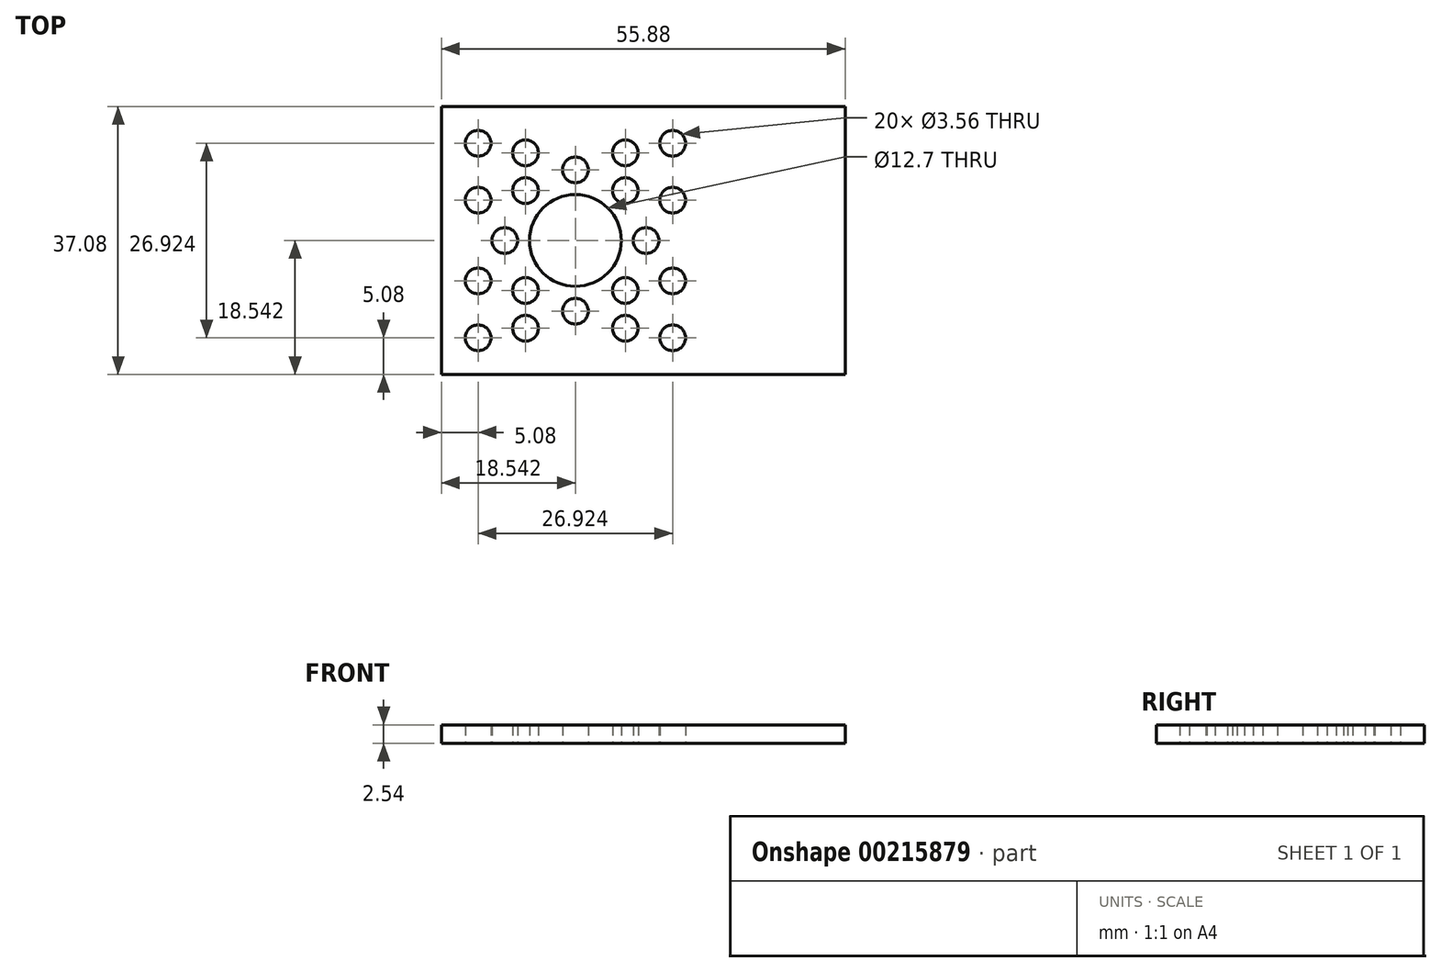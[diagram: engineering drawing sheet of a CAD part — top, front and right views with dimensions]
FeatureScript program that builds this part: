
annotation { "Feature Type Name" : "Feature", "Feature Type Description" : "" }
export const myFeature = defineFeature(function(context is Context, id is Id, definition is map)
    precondition{}
    {
        {
            var Q0;
            Q0=qCreatedBy(makeId("Top.planeOp"),FACE);
            var sketch = newSketch(context, id + "F0", { "sketchPlane" : qUnion([Q0])});
            skLineSegment(sketch, "E0.bottom", {"start": v(0, 0) * mm, "end": v(55.88, 0) * mm});
            skLineSegment(sketch, "E0.top", {"start": v(0, 37.08) * mm, "end": v(55.88, 37.08) * mm});
            skLineSegment(sketch, "E0.left", {"start": v(0, 0) * mm, "end": v(0, 37.08) * mm});
            skLineSegment(sketch, "E0.right", {"start": v(55.88, 0) * mm, "end": v(55.88, 37.08) * mm});
            skCircle(sketch, "E1", {"center": v(18.54, 18.54) * mm, "radius": 6.35 * mm});
            skCircle(sketch, "E2", {"center": v(18.54, 28.32) * mm, "radius": 1.78 * mm});
            skCircle(sketch, "E3", {"center": v(25.45, 30.68) * mm, "radius": 1.78 * mm});
            skCircle(sketch, "E4", {"center": v(25.45, 25.45) * mm, "radius": 1.78 * mm});
            skCircle(sketch, "E5", {"center": v(32, 32) * mm, "radius": 1.78 * mm});
            skCircle(sketch, "E6", {"center": v(32, 24.13) * mm, "radius": 1.78 * mm});
            skLineSegment(sketch, "E7", {"start": v(18.54, 18.54) * mm, "end": v(37.6, 18.54) * mm, "construction": true});
            skLineSegment(sketch, "E8", {"start": v(18.54, 18.54) * mm, "end": v(18.54, 10.07) * mm, "construction": true});
            skCircle(sketch, "E9.MirrorC", {"center": v(11.63, 30.68) * mm, "radius": 1.78 * mm});
            skCircle(sketch, "E10.MirrorC", {"center": v(5.08, 32) * mm, "radius": 1.78 * mm});
            skCircle(sketch, "E11.MirrorC", {"center": v(8.76, 18.54) * mm, "radius": 1.78 * mm});
            skCircle(sketch, "E12.MirrorC", {"center": v(11.63, 25.45) * mm, "radius": 1.78 * mm});
            skCircle(sketch, "E13.MirrorC", {"center": v(5.08, 24.13) * mm, "radius": 1.78 * mm});
            skCircle(sketch, "E14.MirrorC", {"center": v(5.08, 5.08) * mm, "radius": 1.78 * mm});
            skCircle(sketch, "E15.MirrorC", {"center": v(18.54, 8.76) * mm, "radius": 1.78 * mm});
            skCircle(sketch, "E16.MirrorC", {"center": v(11.63, 11.63) * mm, "radius": 1.78 * mm});
            skCircle(sketch, "E17.MirrorC", {"center": v(25.45, 6.4) * mm, "radius": 1.78 * mm});
            skCircle(sketch, "E18.MirrorC", {"center": v(11.63, 6.4) * mm, "radius": 1.78 * mm});
            skCircle(sketch, "E19.MirrorC", {"center": v(25.45, 11.63) * mm, "radius": 1.78 * mm});
            skCircle(sketch, "E20.MirrorC", {"center": v(32, 5.08) * mm, "radius": 1.78 * mm});
            skCircle(sketch, "E21.MirrorC", {"center": v(5.08, 12.95) * mm, "radius": 1.78 * mm});
            skCircle(sketch, "E22.MirrorC", {"center": v(32, 12.95) * mm, "radius": 1.78 * mm});
            skCircle(sketch, "E23.MirrorC", {"center": v(28.32, 18.54) * mm, "radius": 1.78 * mm});
            skLineSegment(sketch, "E24", {"start": v(18.54, 18.54) * mm, "end": v(18.54, -0.5) * mm, "construction": true});
            skSolve(sketch);
        }
        {
            var Q0;
            Q0=qSketchRegion(id+"F0",true);
            extrude(context, id + "F1", {"entities" : qUnion([Q0]), "depth" : 2.54 * mm});
        }
    });
